# Revit family: SDP-856_RV17_LOD_400
name_source: partatom
category: Электрооборудование
revit_build: Autodesk Revit 2017 (Build: 20170118_1100(x64)
units: mm (PartAtom-declared; Revit-internal decimal feet)

## family parameters
Всегда вертикально = Нет
Конфигурация панели = Два столбца, слева направо
На основе рабочей плоскости = Да
Общий = Нет
При загрузке вырезать с полостями = Нет
Размер круглого соединителя = Использовать диаметр
Тип детали = Щит
Точка расчета площади = Нет

## types (1)
- SDP-856
    ADSK_URL страницы изделия = https://stilsoft.ru
    ADSK_Единица измерения = шт.
    ADSK_Завод-изготовитель = ООО «Основа Безопасности»
    ADSK_Количество = 1
    ADSK_Марка = СТАЕ.426459.037-06
    ADSK_Масса = 3
    ADSK_Наименование = IP-видеокамера SDP-856
    Габаритные размеры без кронштейном, мм = 403x163x140
    Габаритные размеры с кронштейном, мм = 450x255x140
    Горизонтальные углы обзора, ˚ = 40,53-8,49
    Диапазон изменения диафрагмы = F2-360
    Диапазон рабочих температур, °С = от –40 до +50
    Максимальное разрешение, пикс = 2592х1944
    Матрица = 1/1,8" Progressive Scan CMOS
    Мощность = 10
    Напряжение = 12
    Объектив = Вариофокальный с автодиафрагмой
    Отметка по умолчанию = 1219 мм
    Поддерживаемые сетевые протоколы = IPv4/IPv6, RTSP/RTP/RTCP, TCP/UDP, HTTP, DHCP, DNS, FTP, DDNS, PPPoE, SMTP, QOS, HTTPS, 802.1x, SNMP, ONVIF2.6.1
    Режим день/ночь = Механический ИК-фильтр с автопереключением
    Сетевой интерфейс = 1 RJ45 10М/100М Ethernet порт
    Сжатие изображения = Н.265/ H.264 /MJPEG
    Скорость передачи = 50Kбит/с~12Mбит/с
    Скорость электронного затвора, с = 1/5 – 1/50000
    Тип крепления объектива = C/CS
    Управление = Веб-интерфейс ,Stil-VS
    Фокусное расстояние объектива, мм = 10-50
    Чувствительность при светосиле F1.2, Люкс (Цвет) = 0.01
    Чувствительность при светосиле F1.2, Люкс (ч/б) = 0.001
